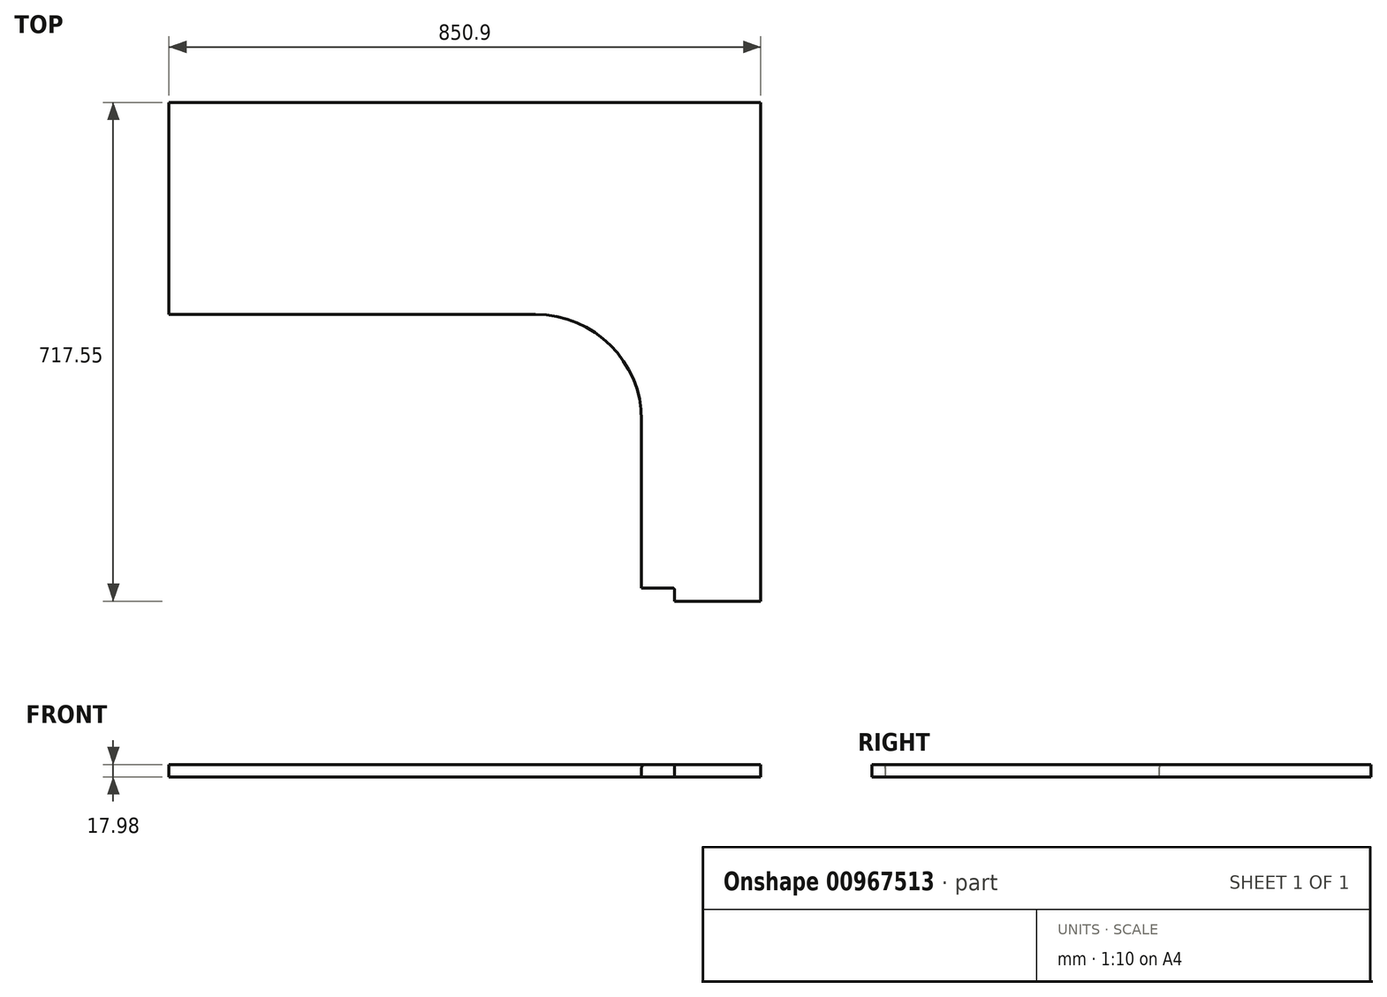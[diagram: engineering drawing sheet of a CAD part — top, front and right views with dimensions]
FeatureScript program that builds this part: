
annotation { "Feature Type Name" : "Feature", "Feature Type Description" : "" }
export const myFeature = defineFeature(function(context is Context, id is Id, definition is map)
    precondition{}
    {
        {
            var Q0;
            Q0=qCreatedBy(makeId("Top.planeOp"),FACE);
            var sketch = newSketch(context, id + "F0", { "sketchPlane" : qUnion([Q0])});
            skLineSegment(sketch, "E0.bottom", {"start": v(-123.82, -717.55) * mm, "end": v(0, -717.55) * mm});
            skLineSegment(sketch, "E0.top", {"start": v(-850.9, 0) * mm, "end": v(0, 0) * mm});
            skLineSegment(sketch, "E0.left", {"start": v(-850.9, -304.8) * mm, "end": v(-850.9, 0) * mm});
            skLineSegment(sketch, "E0.right", {"start": v(0, -717.55) * mm, "end": v(0, 0) * mm});
            skLineSegment(sketch, "E1", {"start": v(-850.9, -304.8) * mm, "end": v(-171.45, -304.8) * mm});
            skLineSegment(sketch, "E2", {"start": v(-171.45, -304.8) * mm, "end": v(-171.45, -698.5) * mm});
            skLineSegment(sketch, "E3", {"start": v(-171.45, -698.5) * mm, "end": v(-123.82, -698.5) * mm});
            skLineSegment(sketch, "E4", {"start": v(-123.82, -698.5) * mm, "end": v(-123.82, -717.55) * mm});
            skSolve(sketch);
        }
        {
            var Q0;
            Q0=makeQuery(id+"F0.imprint","IMPRINT",FACE,{"disambiguationData":[TD([[makeQuery(id+"F0.imprint","IMPRINT",EDGE,{"derivedFrom":sQuery(id+"F0.wireOp",EDGE,"E0.bottom")}),1.0]])]});
            extrude(context, id + "F1", {"entities" : qUnion([Q0]), "depth" : 17.98 * mm, "offsetDistance" : 25.4 * mm});
        }
        {
            var Q0;
            Q0=makeQuery(id+"F1.opExtrude","SWEPT_EDGE",EDGE,{"disambiguationData":[OSD([sQuery(id+"F0.wireOp",EDGE,"E1"),sQuery(id+"F0.wireOp",EDGE,"E2")])]});
            fillet(context, id + "F2", {"entities" : qUnion([Q0]), "radius" : 152.4 * mm, "tangentPropagation" : true, "allowEdgeOverflow" : false});
        }
        {
            var Q0;
            Q0=makeQuery(id+"F1.opExtrude","SWEPT_EDGE",EDGE,{"disambiguationData":[OSD([sQuery(id+"F0.wireOp",EDGE,"E3"),sQuery(id+"F0.wireOp",EDGE,"E4")])]});
            fillet(context, id + "F3", {"entities" : qUnion([Q0]), "radius" : 3.3 * mm, "tangentPropagation" : true, "allowEdgeOverflow" : false});
        }
        {
            var Q0;
            Q0=makeQuery(id+"F1.opExtrude","CAP_EDGE",EDGE,{"disambiguationData":[OSD([sQuery(id+"F0.wireOp",EDGE,"E2")])],"isStart":false});
            fillet(context, id + "F4", {"entities" : qUnion([Q0]), "radius" : 5.08 * mm, "tangentPropagation" : true, "allowEdgeOverflow" : false});
        }
    });
